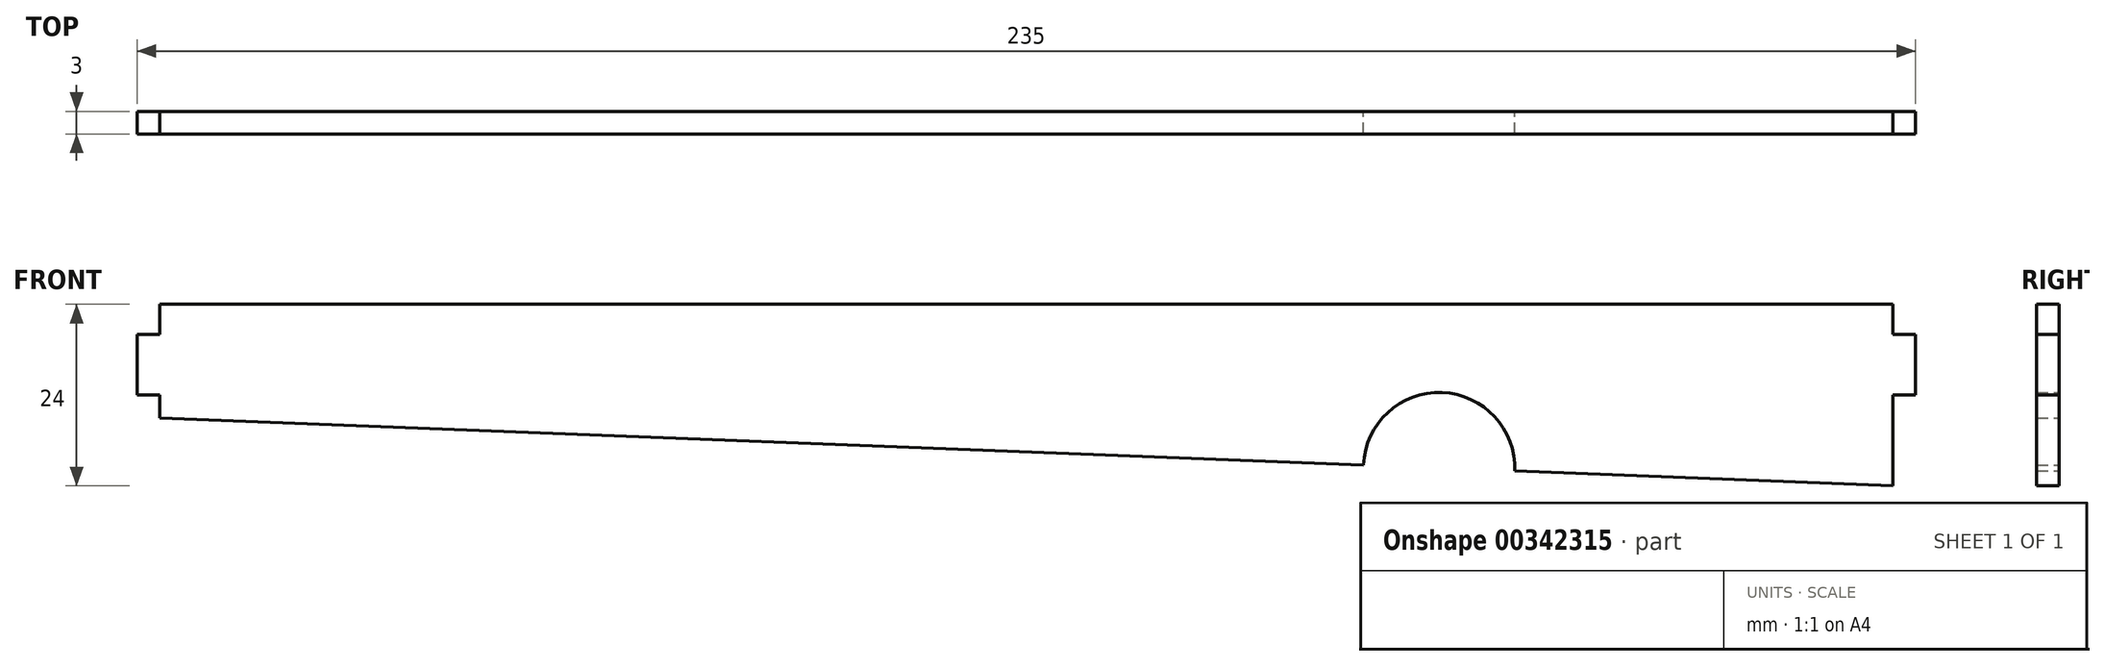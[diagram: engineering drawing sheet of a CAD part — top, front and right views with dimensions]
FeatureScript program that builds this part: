
annotation { "Feature Type Name" : "Feature", "Feature Type Description" : "" }
export const myFeature = defineFeature(function(context is Context, id is Id, definition is map)
    precondition{}
    {
        {
            var Q0;
            Q0=qCreatedBy(makeId("Front.planeOp"),FACE);
            var sketch = newSketch(context, id + "F0", { "sketchPlane" : qUnion([Q0])});
            skLineSegment(sketch, "E0.bottom", {"start": v(0, 0) * mm, "end": v(229, -9) * mm, "construction": true});
            skLineSegment(sketch, "E0.top", {"start": v(0, 15) * mm, "end": v(229, 15) * mm});
            skLineSegment(sketch, "E1.bottom", {"start": v(0, 11) * mm, "end": v(-3, 11) * mm});
            skLineSegment(sketch, "E1.top", {"start": v(0, 3) * mm, "end": v(-3, 3) * mm});
            skLineSegment(sketch, "E1.right", {"start": v(-3, 11) * mm, "end": v(-3, 3) * mm});
            skLineSegment(sketch, "E2.bottom", {"start": v(229, 11) * mm, "end": v(232, 11) * mm});
            skLineSegment(sketch, "E2.top", {"start": v(229, 3) * mm, "end": v(232, 3) * mm});
            skLineSegment(sketch, "E2.right", {"start": v(232, 11) * mm, "end": v(232, 3) * mm});
            skLineSegment(sketch, "E3", {"start": v(0, 15) * mm, "end": v(0, 11) * mm});
            skLineSegment(sketch, "E4", {"start": v(0, 3) * mm, "end": v(0, 0) * mm});
            skLineSegment(sketch, "E5", {"start": v(229, 15) * mm, "end": v(229, 11) * mm});
            skLineSegment(sketch, "E6", {"start": v(229, 3) * mm, "end": v(229, -9) * mm});
            skArc(sketch, "E7", {"start": v(159.05, -6.25) * mm, "mid": v(169.44, 3.35) * mm, "end": v(179.04, -7.04) * mm});
            skLineSegment(sketch, "E8", {"start": v(0, 0) * mm, "end": v(159.05, -6.25) * mm});
            skLineSegment(sketch, "E9", {"start": v(179.04, -7.04) * mm, "end": v(229, -9) * mm});
            skSolve(sketch);
        }
        {
            var Q0;
            Q0=makeQuery(id+"F0.imprint","IMPRINT",FACE,{"disambiguationData":[TD([[makeQuery(id+"F0.imprint","IMPRINT",EDGE,{"derivedFrom":sQuery(id+"F0.wireOp",EDGE,"E0.top")}),-1.0]])]});
            extrude(context, id + "F1", {"entities" : qUnion([Q0]), "depth" : 3 * mm, "offsetDistance" : 25 * mm});
        }
    });
